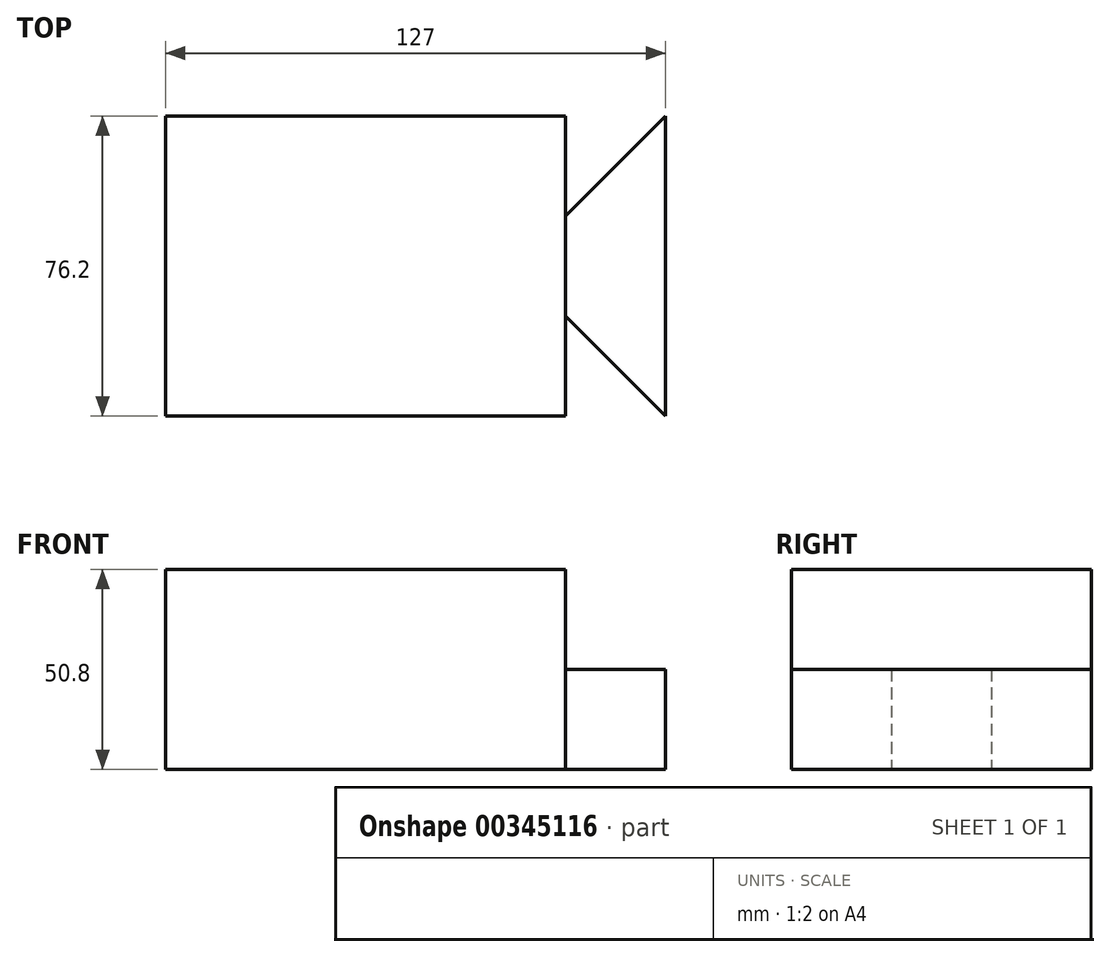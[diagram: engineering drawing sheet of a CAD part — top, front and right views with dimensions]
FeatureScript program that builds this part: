
annotation { "Feature Type Name" : "Feature", "Feature Type Description" : "" }
export const myFeature = defineFeature(function(context is Context, id is Id, definition is map)
    precondition{}
    {
        {
            var Q0;
            Q0=qCreatedBy(makeId("Top.planeOp"),FACE);
            var sketch = newSketch(context, id + "F0", { "sketchPlane" : qUnion([Q0])});
            skLineSegment(sketch, "E0", {"start": v(0, 0) * mm, "end": v(0, 76.2) * mm});
            skLineSegment(sketch, "E1", {"start": v(0, 76.2) * mm, "end": v(101.6, 76.2) * mm});
            skLineSegment(sketch, "E2", {"start": v(101.6, 76.2) * mm, "end": v(101.6, 50.8) * mm});
            skLineSegment(sketch, "E3", {"start": v(101.6, 50.8) * mm, "end": v(127, 76.2) * mm});
            skLineSegment(sketch, "E4", {"start": v(127, 76.2) * mm, "end": v(127, 0) * mm});
            skLineSegment(sketch, "E5", {"start": v(127, 0) * mm, "end": v(101.6, 25.4) * mm});
            skLineSegment(sketch, "E6", {"start": v(101.6, 25.4) * mm, "end": v(101.6, 0) * mm});
            skLineSegment(sketch, "E7", {"start": v(101.6, 0) * mm, "end": v(0, 0) * mm});
            skSolve(sketch);
        }
        {
            var Q0;
            Q0=makeQuery(id+"F0.imprint","IMPRINT",FACE,{"disambiguationData":[TD([[makeQuery(id+"F0.imprint","IMPRINT",EDGE,{"derivedFrom":sQuery(id+"F0.wireOp",EDGE,"E0")}),-1.0]])]});
            extrude(context, id + "F1", {"entities" : qUnion([Q0]), "depth" : 50.8 * mm});
        }
        {
            var Q0;
            Q0=makeQuery(id+"F1.opExtrude","CAP_FACE",FACE,{"disambiguationData":[OSD([sQuery(id+"F0.wireOp",EDGE,"E0"),sQuery(id+"F0.wireOp",EDGE,"E1"),sQuery(id+"F0.wireOp",EDGE,"E2"),sQuery(id+"F0.wireOp",EDGE,"E3"),sQuery(id+"F0.wireOp",EDGE,"E4"),sQuery(id+"F0.wireOp",EDGE,"E5"),sQuery(id+"F0.wireOp",EDGE,"E6"),sQuery(id+"F0.wireOp",EDGE,"E7")])],"isStart":false});
            var sketch = newSketch(context, id + "F2", { "sketchPlane" : qUnion([Q0])});
            skLineSegment(sketch, "E8", {"start": v(101.6, 25.4) * mm, "end": v(101.6, 50.8) * mm});
            skLineSegment(sketch, "E9", {"start": v(101.6, 50.8) * mm, "end": v(127, 76.2) * mm});
            skLineSegment(sketch, "E10", {"start": v(127, 76.2) * mm, "end": v(127, 0) * mm});
            skLineSegment(sketch, "E11", {"start": v(127, 0) * mm, "end": v(101.6, 25.4) * mm});
            skSolve(sketch);
        }
        {
            var Q0;
            Q0 = qSketchRegion(id + "F2", true);
            extrude(context, id + "F3", {"entities" : qUnion([Q0]), "operationType" : NewBodyOperationType.REMOVE, "oppositeDirection" : true, "depth" : 25.4 * mm});
        }
    });
